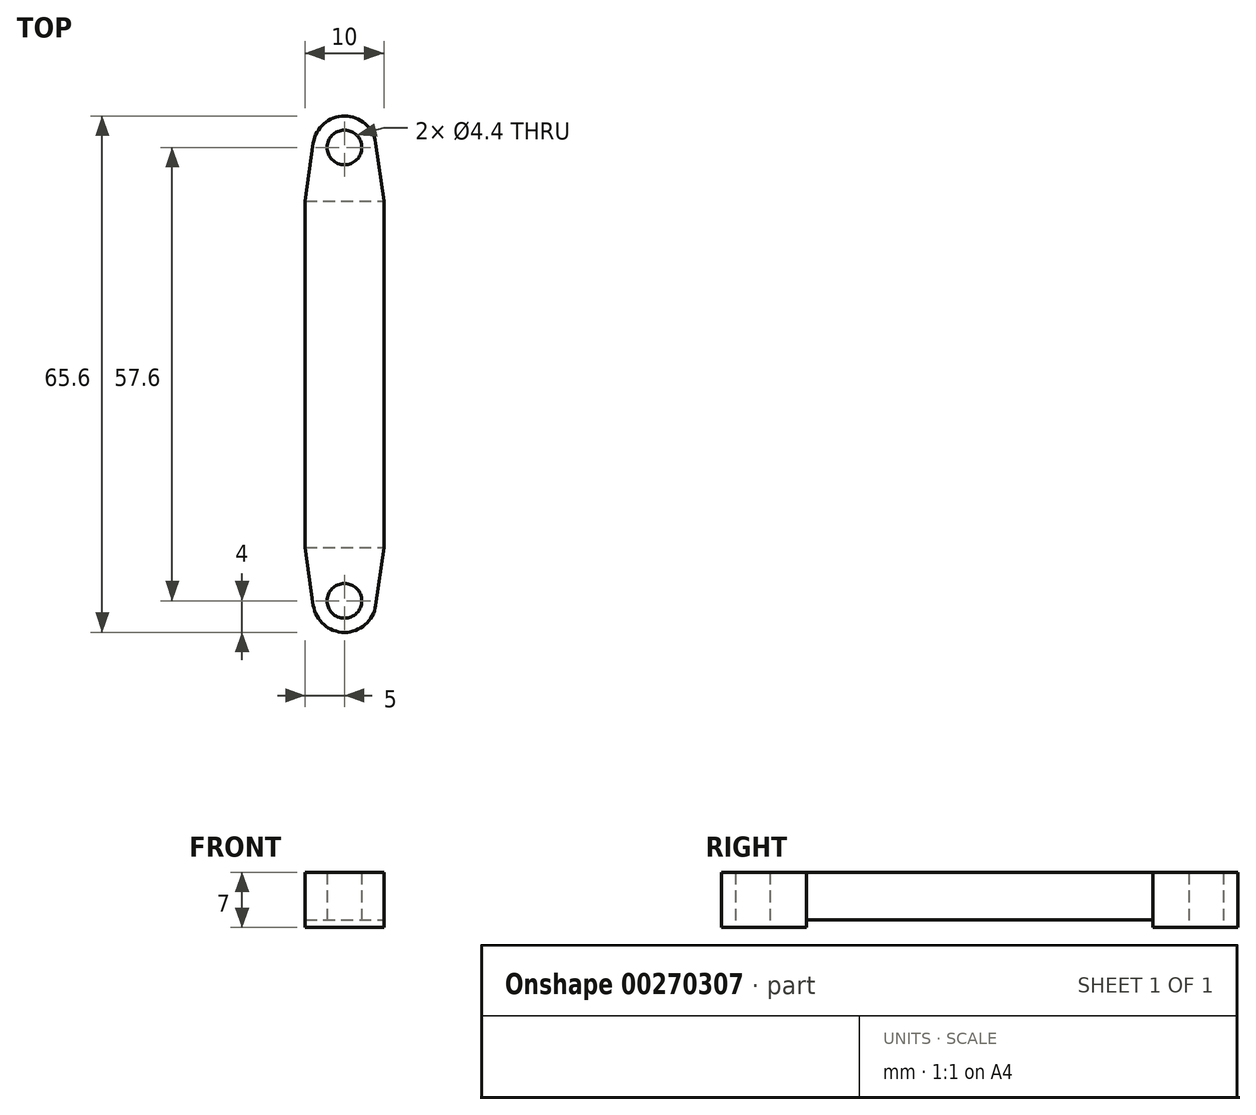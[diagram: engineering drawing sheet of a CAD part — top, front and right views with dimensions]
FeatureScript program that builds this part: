
annotation { "Feature Type Name" : "Feature", "Feature Type Description" : "" }
export const myFeature = defineFeature(function(context is Context, id is Id, definition is map)
    precondition{}
    {
        {
            var Q0;
            Q0=qCreatedBy(makeId("Top.planeOp"),FACE);
            var sketch = newSketch(context, id + "F0", { "sketchPlane" : qUnion([Q0])});
            skLineSegment(sketch, "E0.bottom", {"start": v(-5, 22) * mm, "end": v(5, 22) * mm});
            skLineSegment(sketch, "E0.top", {"start": v(-5, -22) * mm, "end": v(5, -22) * mm});
            skLineSegment(sketch, "E0.left", {"start": v(-5, 22) * mm, "end": v(-5, -22) * mm});
            skLineSegment(sketch, "E0.right", {"start": v(5, 22) * mm, "end": v(5, -22) * mm});
            skPoint(sketch, "E1", {"position": v(5, 0) * mm});
            skPoint(sketch, "E2", {"position": v(0, 22) * mm});
            skPoint(sketch, "E3", {"position": v(0, 28.8) * mm});
            skPoint(sketch, "E4", {"position": v(0, -28.8) * mm});
            skLineSegment(sketch, "E5", {"start": v(0, 28.8) * mm, "end": v(0, -28.8) * mm, "construction": true});
            skCircle(sketch, "E6", {"center": v(0, 28.8) * mm, "radius": 2 * mm});
            skCircle(sketch, "E7", {"center": v(0, -28.8) * mm, "radius": 2 * mm});
            skCircle(sketch, "E8", {"center": v(0, 28.8) * mm, "radius": 4 * mm});
            skCircle(sketch, "E9", {"center": v(0, -28.8) * mm, "radius": 4 * mm});
            skLineSegment(sketch, "E10", {"start": v(-5, 22) * mm, "end": v(-3.96, 29.36) * mm});
            skLineSegment(sketch, "E11", {"start": v(5, 22) * mm, "end": v(3.96, 29.36) * mm});
            skLineSegment(sketch, "E12", {"start": v(-5, -22) * mm, "end": v(-3.96, -29.36) * mm});
            skLineSegment(sketch, "E13", {"start": v(5, -22) * mm, "end": v(3.96, -29.36) * mm});
            skSolve(sketch);
        }
        {
            var Q0;
            Q0=makeQuery(id+"F0.imprint","IMPRINT",FACE,{"disambiguationData":[TD([[makeQuery(id+"F0.imprint","IMPRINT",EDGE,{"derivedFrom":sQuery(id+"F0.wireOp",EDGE,"E6")}),1.0]])]});
            var Q1;
            Q1=makeQuery(id+"F0.imprint","IMPRINT",FACE,{"disambiguationData":[TD([[makeQuery(id+"F0.imprint","IMPRINT",EDGE,{"derivedFrom":sQuery(id+"F0.wireOp",EDGE,"E6")}),-1.0]])]});
            var Q2;
            Q2=makeQuery(id+"F0.imprint","IMPRINT",FACE,{"disambiguationData":[TD([[makeQuery(id+"F0.imprint","IMPRINT",EDGE,{"derivedFrom":sQuery(id+"F0.wireOp",EDGE,"E0.bottom")}),1.0]])]});
            var Q3;
            Q3=makeQuery(id+"F0.imprint","IMPRINT",FACE,{"disambiguationData":[TD([[makeQuery(id+"F0.imprint","IMPRINT",EDGE,{"derivedFrom":sQuery(id+"F0.wireOp",EDGE,"E0.bottom")}),-1.0]])]});
            var Q4;
            Q4=makeQuery(id+"F0.imprint","IMPRINT",FACE,{"disambiguationData":[TD([[makeQuery(id+"F0.imprint","IMPRINT",EDGE,{"derivedFrom":sQuery(id+"F0.wireOp",EDGE,"E0.top")}),-1.0]])]});
            var Q5;
            Q5=makeQuery(id+"F0.imprint","IMPRINT",FACE,{"disambiguationData":[TD([[makeQuery(id+"F0.imprint","IMPRINT",EDGE,{"derivedFrom":sQuery(id+"F0.wireOp",EDGE,"E7")}),-1.0]])]});
            var Q6;
            Q6=makeQuery(id+"F0.imprint","IMPRINT",FACE,{"disambiguationData":[TD([[makeQuery(id+"F0.imprint","IMPRINT",EDGE,{"derivedFrom":sQuery(id+"F0.wireOp",EDGE,"E7")}),1.0]])]});
            extrude(context, id + "F1", {"entities" : qUnion([Q0, Q1, Q2, Q3, Q4, Q5, Q6]), "depth" : 6 * mm});
        }
        {
            var Q0;
            Q0=makeQuery(id+"F0.imprint","IMPRINT",FACE,{"disambiguationData":[TD([[makeQuery(id+"F0.imprint","IMPRINT",EDGE,{"derivedFrom":sQuery(id+"F0.wireOp",EDGE,"E0.bottom")}),1.0]])]});
            var Q1;
            Q1=makeQuery(id+"F0.imprint","IMPRINT",FACE,{"disambiguationData":[TD([[makeQuery(id+"F0.imprint","IMPRINT",EDGE,{"derivedFrom":sQuery(id+"F0.wireOp",EDGE,"E6")}),-1.0]])]});
            var Q2;
            Q2=makeQuery(id+"F0.imprint","IMPRINT",FACE,{"disambiguationData":[TD([[makeQuery(id+"F0.imprint","IMPRINT",EDGE,{"derivedFrom":sQuery(id+"F0.wireOp",EDGE,"E6")}),1.0]])]});
            var Q3;
            Q3=makeQuery(id+"F0.imprint","IMPRINT",FACE,{"disambiguationData":[TD([[makeQuery(id+"F0.imprint","IMPRINT",EDGE,{"derivedFrom":sQuery(id+"F0.wireOp",EDGE,"E0.top")}),-1.0]])]});
            var Q4;
            Q4=makeQuery(id+"F0.imprint","IMPRINT",FACE,{"disambiguationData":[TD([[makeQuery(id+"F0.imprint","IMPRINT",EDGE,{"derivedFrom":sQuery(id+"F0.wireOp",EDGE,"E7")}),-1.0]])]});
            var Q5;
            Q5=makeQuery(id+"F0.imprint","IMPRINT",FACE,{"disambiguationData":[TD([[makeQuery(id+"F0.imprint","IMPRINT",EDGE,{"derivedFrom":sQuery(id+"F0.wireOp",EDGE,"E7")}),1.0]])]});
            extrude(context, id + "F2", {"entities" : qUnion([Q0, Q1, Q2, Q3, Q4, Q5]), "operationType" : NewBodyOperationType.ADD, "oppositeDirection" : true, "depth" : 1 * mm});
        }
        {
            var Q0;
            Q0=sQuery(id+"F0.wireOp",VERTEX,"E3");
            var Q1;
            Q1=sQuery(id+"F0.wireOp",VERTEX,"E4");
            var Q2;
            Q2=makeQuery(id+"F1.opExtrude","SWEPT_BODY",BODY,{"disambiguationData":[OSD([sQuery(id+"F0.wireOp",EDGE,"E0.left"),sQuery(id+"F0.wireOp",EDGE,"E0.right"),sQuery(id+"F0.wireOp",EDGE,"E8"),sQuery(id+"F0.wireOp",EDGE,"E9"),sQuery(id+"F0.wireOp",EDGE,"E10"),sQuery(id+"F0.wireOp",EDGE,"E11"),sQuery(id+"F0.wireOp",EDGE,"E12"),sQuery(id+"F0.wireOp",EDGE,"E13")])]});
            hole(context, id + "F3", {"style" : HoleStyle.SIMPLE, "endStyle" : HoleEndStyle.THROUGH, "oppositeDirection" : true, "standardTappedOrClearance" : lookupTablePath({ "standard" : "ISO", "fit" : "Normal", "size" : "M4", "type" : "Clearance" }), "standardBlindInLast" : lookupTablePath({ "fit" : "Standard", "standard" : "ISO", "size" : "M4", "type" : "Clearance" }), "holeDiameter" : 4.4 * mm, "tappedDepth" : 12 * mm, "tapClearance" : 3, "locations" : qUnion([Q0, Q1]), "scope" : qUnion([Q2])});
        }
        {
            var Q0;
            Q0=sQuery(id+"F0.wireOp",VERTEX,"E3");
            var Q1;
            Q1=sQuery(id+"F0.wireOp",VERTEX,"E4");
            var Q2;
            Q2=makeQuery(id+"F1.opExtrude","SWEPT_BODY",BODY,{"disambiguationData":[OSD([sQuery(id+"F0.wireOp",EDGE,"E0.left"),sQuery(id+"F0.wireOp",EDGE,"E0.right"),sQuery(id+"F0.wireOp",EDGE,"E8"),sQuery(id+"F0.wireOp",EDGE,"E9"),sQuery(id+"F0.wireOp",EDGE,"E10"),sQuery(id+"F0.wireOp",EDGE,"E11"),sQuery(id+"F0.wireOp",EDGE,"E12"),sQuery(id+"F0.wireOp",EDGE,"E13")])]});
            hole(context, id + "F4", {"style" : HoleStyle.SIMPLE, "endStyle" : HoleEndStyle.THROUGH, "standardTappedOrClearance" : lookupTablePath({ "standard" : "ISO", "fit" : "Normal", "size" : "M4", "type" : "Clearance" }), "standardBlindInLast" : lookupTablePath({ "fit" : "Standard", "standard" : "ISO", "size" : "M4", "type" : "Clearance" }), "holeDiameter" : 4.4 * mm, "tappedDepth" : 12 * mm, "tapClearance" : 3, "locations" : qUnion([Q0, Q1]), "scope" : qUnion([Q2])});
        }
    });
